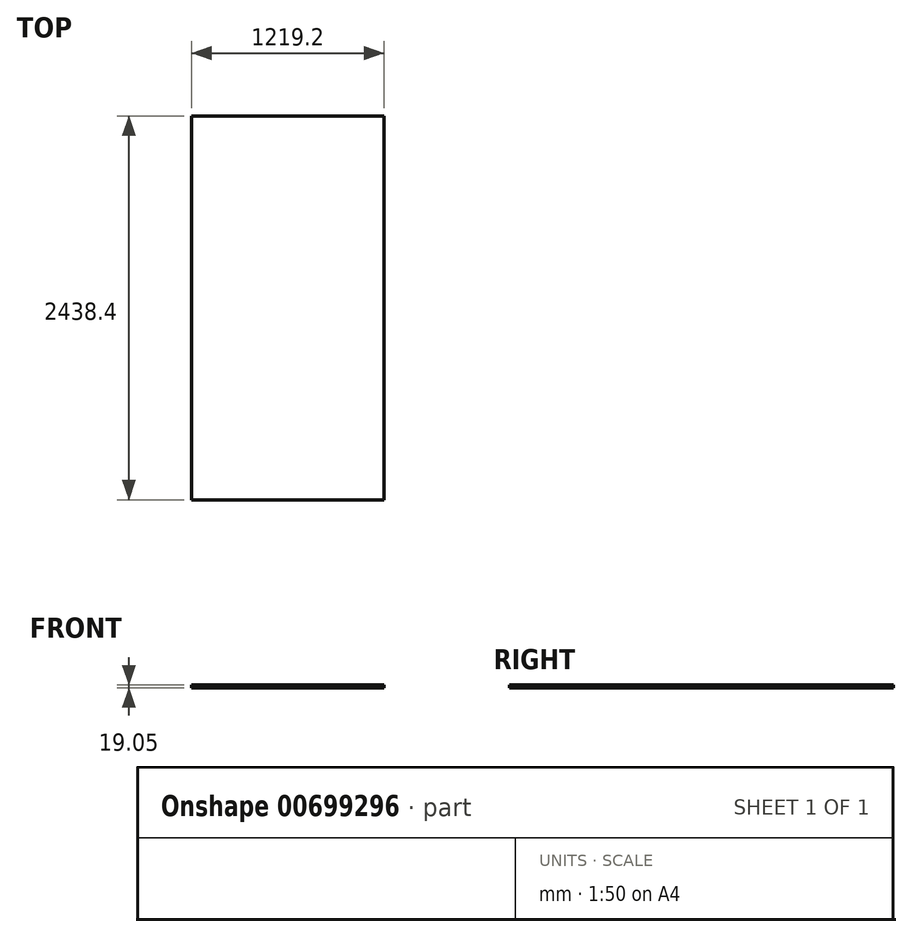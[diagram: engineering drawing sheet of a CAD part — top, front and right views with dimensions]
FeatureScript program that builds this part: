
annotation { "Feature Type Name" : "Feature", "Feature Type Description" : "" }
export const myFeature = defineFeature(function(context is Context, id is Id, definition is map)
    precondition{}
    {
        {
            var Q0;
            Q0=qCreatedBy(makeId("Front.planeOp"),FACE);
            var sketch = newSketch(context, id + "F0", { "sketchPlane" : qUnion([Q0])});
            skLineSegment(sketch, "E0.bottom", {"start": v(-618.13, -63.17) * mm, "end": v(601.07, -63.17) * mm});
            skLineSegment(sketch, "E0.top", {"start": v(-618.13, -82.22) * mm, "end": v(601.07, -82.22) * mm});
            skLineSegment(sketch, "E0.left", {"start": v(-618.13, -63.17) * mm, "end": v(-618.13, -82.22) * mm});
            skLineSegment(sketch, "E0.right", {"start": v(601.07, -63.17) * mm, "end": v(601.07, -82.22) * mm});
            skSolve(sketch);
        }
        {
            var Q0;
            Q0=qSketchRegion(id+"F0",true);
            extrude(context, id + "F1", {"entities" : qUnion([Q0]), "endBound" : BoundingType.SYMMETRIC, "depth" : 2438.4 * mm});
        }
    });
